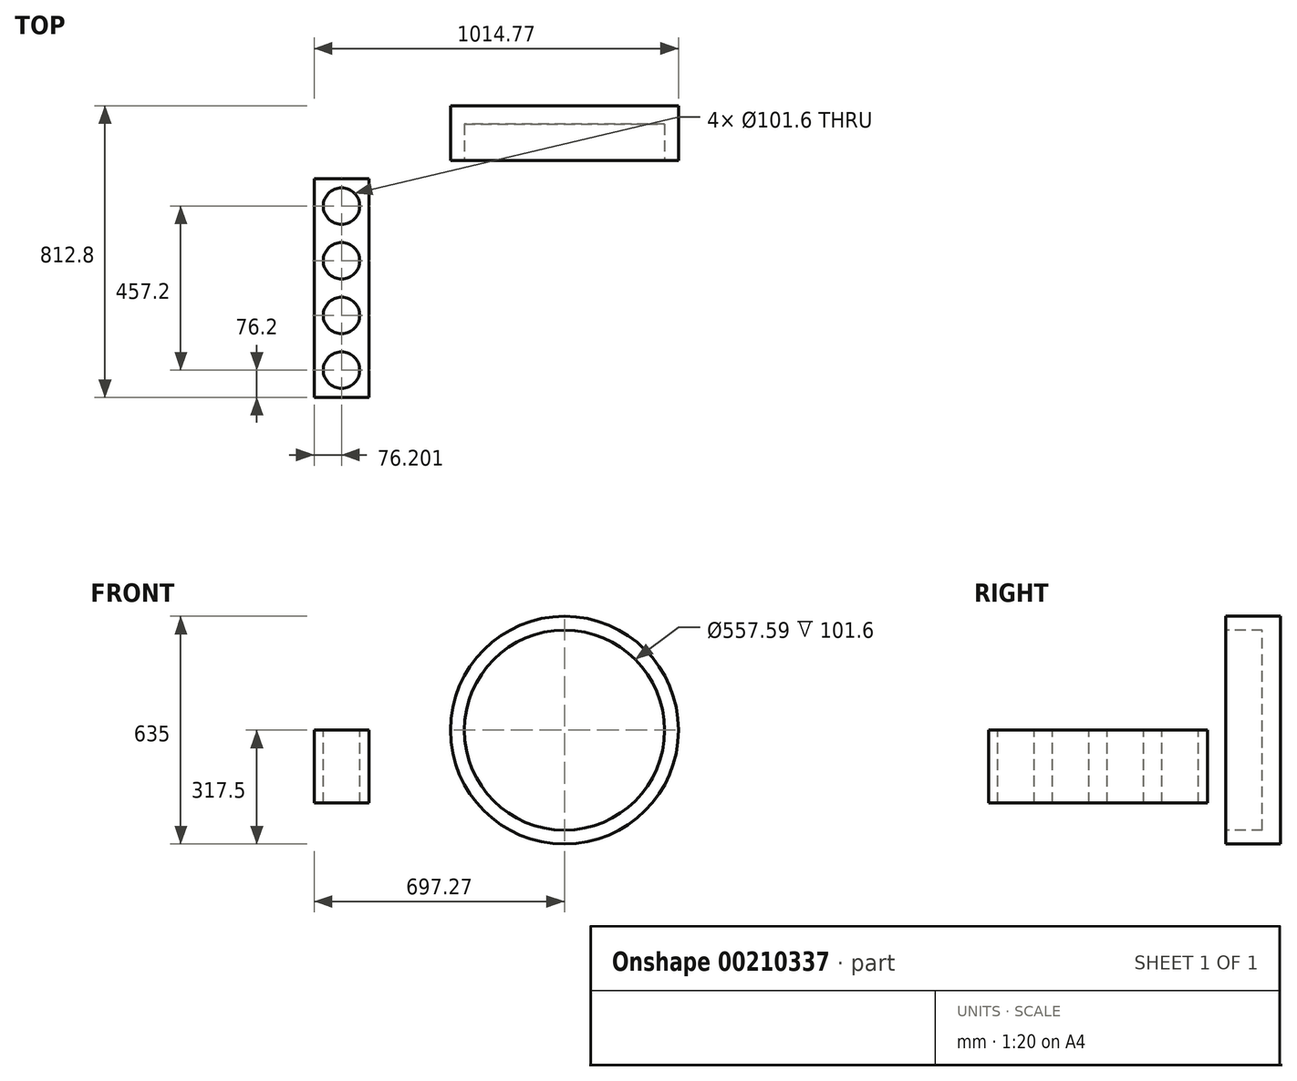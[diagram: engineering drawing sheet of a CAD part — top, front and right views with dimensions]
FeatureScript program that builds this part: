
annotation { "Feature Type Name" : "Feature", "Feature Type Description" : "" }
export const myFeature = defineFeature(function(context is Context, id is Id, definition is map)
    precondition{}
    {
        {
            var Q0;
            Q0=qCreatedBy(makeId("Front.planeOp"),FACE);
            var sketch = newSketch(context, id + "F0", { "sketchPlane" : qUnion([Q0])});
            skCircle(sketch, "E0", {"center": v(0, 0) * mm, "radius": 317.5 * mm});
            skSolve(sketch);
        }
        {
            var Q0;
            Q0 = qSketchRegion(id + "F0", true);
            extrude(context, id + "F1", {"entities" : qUnion([Q0]), "depth" : 152.4 * mm});
        }
        {
            var Q0;
            Q0=qCreatedBy(makeId("Top.planeOp"),FACE);
            var sketch = newSketch(context, id + "F2", { "sketchPlane" : qUnion([Q0])});
            skLineSegment(sketch, "E1.bottom", {"start": v(-544.87, -203.2) * mm, "end": v(-697.27, -203.2) * mm});
            skLineSegment(sketch, "E1.top", {"start": v(-544.87, -812.8) * mm, "end": v(-697.27, -812.8) * mm});
            skLineSegment(sketch, "E1.left", {"start": v(-544.87, -203.2) * mm, "end": v(-544.87, -812.8) * mm});
            skLineSegment(sketch, "E1.right", {"start": v(-697.27, -203.2) * mm, "end": v(-697.27, -812.8) * mm});
            skCircle(sketch, "E2", {"center": v(-621.07, -279.4) * mm, "radius": 50.8 * mm});
            skCircle(sketch, "E3.0.1.0", {"center": v(-621.07, -431.8) * mm, "radius": 50.8 * mm});
            skCircle(sketch, "E3.0.2.0", {"center": v(-621.07, -584.2) * mm, "radius": 50.8 * mm});
            skCircle(sketch, "E3.0.3.0", {"center": v(-621.07, -736.6) * mm, "radius": 50.8 * mm});
            skLineSegment(sketch, "E3.direction1", {"start": v(-621.07, -279.4) * mm, "end": v(-595.67, -279.4) * mm, "construction": true});
            skLineSegment(sketch, "E3.direction2", {"start": v(-621.07, -279.4) * mm, "end": v(-621.07, -431.8) * mm, "construction": true});
            skSolve(sketch);
        }
        {
            var Q0;
            Q0 = qSketchRegion(id + "F2", true);
            extrude(context, id + "F3", {"entities" : qUnion([Q0]), "oppositeDirection" : true, "depth" : 203.2 * mm});
        }
        {
            var Q0;
            Q0=makeQuery(id+"F1.opExtrude","CAP_FACE",FACE,{"disambiguationData":[OSD([sQuery(id+"F0.wireOp",EDGE,"E0")])],"isStart":false});
            var sketch = newSketch(context, id + "F4", { "sketchPlane" : qUnion([Q0])});
            skCircle(sketch, "E4", {"center": v(0, 0) * mm, "radius": 278.8 * mm});
            skSolve(sketch);
        }
        {
            var Q0;
            Q0 = qSketchRegion(id + "F4", true);
            extrude(context, id + "F5", {"entities" : qUnion([Q0]), "operationType" : NewBodyOperationType.REMOVE, "oppositeDirection" : true, "depth" : 101.6 * mm});
        }
    });
